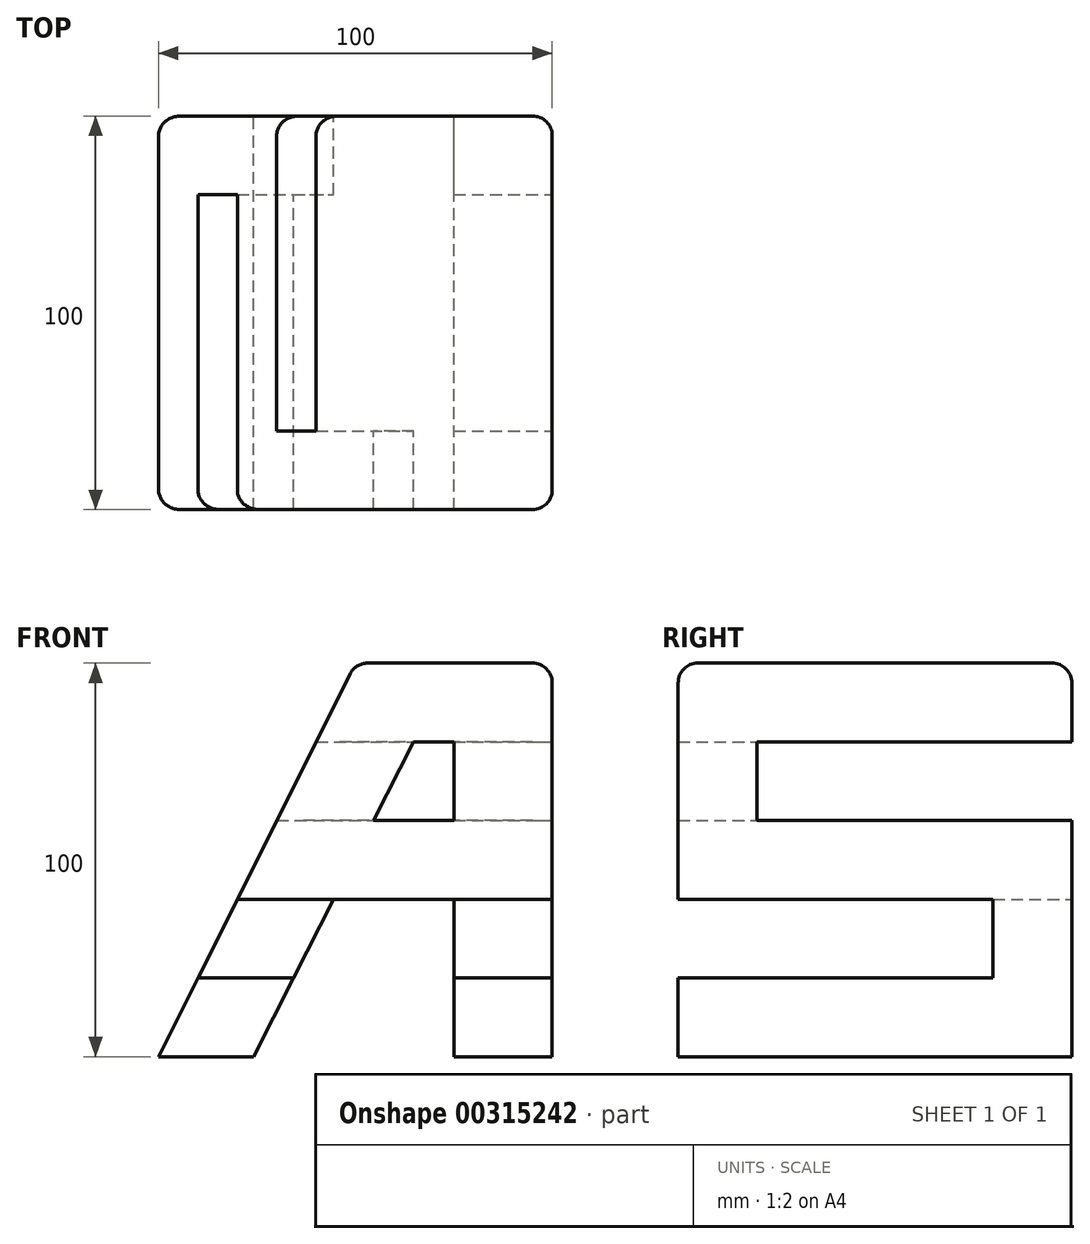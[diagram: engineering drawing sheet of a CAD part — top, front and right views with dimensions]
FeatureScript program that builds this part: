
annotation { "Feature Type Name" : "Feature", "Feature Type Description" : "" }
export const myFeature = defineFeature(function(context is Context, id is Id, definition is map)
    precondition{}
    {
        {
            var Q0;
            Q0=qCreatedBy(makeId("Front.planeOp"),FACE);
            var sketch = newSketch(context, id + "F0", { "sketchPlane" : qUnion([Q0])});
            skLineSegment(sketch, "E0.top", {"start": v(-50, -50) * mm, "end": v(-25.92, -50) * mm});
            skLineSegment(sketch, "E0.right", {"start": v(50, 50) * mm, "end": v(50, 30) * mm});
            skPoint(sketch, "E0.middle", {"position": v(0, 0) * mm});
            skLineSegment(sketch, "E1", {"start": v(0, 50) * mm, "end": v(25, 50) * mm});
            skLineSegment(sketch, "E2", {"start": v(0, 50) * mm, "end": v(-50, -50) * mm});
            skLineSegment(sketch, "E3", {"start": v(25, 50) * mm, "end": v(50, 50) * mm});
            skLineSegment(sketch, "E4", {"start": v(50, -30) * mm, "end": v(50, -50) * mm});
            skLineSegment(sketch, "E5", {"start": v(50, -10) * mm, "end": v(50, -30) * mm});
            skLineSegment(sketch, "E6", {"start": v(50, 10) * mm, "end": v(50, -10) * mm});
            skLineSegment(sketch, "E7", {"start": v(50, 30) * mm, "end": v(50, 10) * mm});
            skLineSegment(sketch, "E8", {"start": v(-5.55, -10) * mm, "end": v(-15.73, -30) * mm});
            skLineSegment(sketch, "E9", {"start": v(-15.73, -30) * mm, "end": v(-25.92, -50) * mm});
            skLineSegment(sketch, "E10", {"start": v(25, 30) * mm, "end": v(25, 10) * mm});
            skLineSegment(sketch, "E11", {"start": v(25, 10) * mm, "end": v(4.63, 10) * mm});
            skLineSegment(sketch, "E12", {"start": v(25, -10) * mm, "end": v(25, -30) * mm});
            skLineSegment(sketch, "E13", {"start": v(25, -30) * mm, "end": v(25, -50) * mm});
            skLineSegment(sketch, "E14", {"start": v(14.82, 30) * mm, "end": v(4.63, 10) * mm});
            skLineSegment(sketch, "E15", {"start": v(25, 30) * mm, "end": v(14.82, 30) * mm});
            skLineSegment(sketch, "E16", {"start": v(25, -10) * mm, "end": v(-5.55, -10) * mm});
            skLineSegment(sketch, "E17", {"start": v(25, -50) * mm, "end": v(50, -50) * mm});
            skSolve(sketch);
        }
        {
            var Q0;
            Q0=makeQuery(id+"F0.imprint","IMPRINT",FACE,{"disambiguationData":[TD([[makeQuery(id+"F0.imprint","IMPRINT",EDGE,{"derivedFrom":sQuery(id+"F0.wireOp",EDGE,"E0.top")}),1.0]])]});
            extrude(context, id + "F1", {"entities" : qUnion([Q0]), "depth" : 100 * mm});
        }
        {
            var Q0;
            Q0=makeQuery(id+"F1.opExtrude","SWEPT_FACE",FACE,{"disambiguationData":[OSD([sQuery(id+"F0.wireOp",EDGE,"E0.right"),sQuery(id+"F0.wireOp",EDGE,"E4"),sQuery(id+"F0.wireOp",EDGE,"E5"),sQuery(id+"F0.wireOp",EDGE,"E6"),sQuery(id+"F0.wireOp",EDGE,"E7")])]});
            var sketch = newSketch(context, id + "F2", { "sketchPlane" : qUnion([Q0])});
            skLineSegment(sketch, "E18.bottom", {"start": v(-100, -30) * mm, "end": v(-20, -30) * mm});
            skLineSegment(sketch, "E18.top", {"start": v(-100, -10) * mm, "end": v(-20, -10) * mm});
            skLineSegment(sketch, "E18.left", {"start": v(-100, -30) * mm, "end": v(-100, -10) * mm});
            skLineSegment(sketch, "E18.right", {"start": v(-20, -30) * mm, "end": v(-20, -10) * mm});
            skSolve(sketch);
        }
        {
            var Q0;
            Q0=makeQuery(id+"F2.imprint","IMPRINT",FACE,{"disambiguationData":[TD([[makeQuery(id+"F2.imprint","IMPRINT",EDGE,{"derivedFrom":sQuery(id+"F2.wireOp",EDGE,"E18.bottom")}),1.0]])]});
            extrude(context, id + "F3", {"entities" : qUnion([Q0]), "operationType" : NewBodyOperationType.REMOVE, "oppositeDirection" : true, "depth" : 100 * mm});
        }
        {
            var Q0;
            Q0=makeQuery(id+"F1.opExtrude","SWEPT_FACE",FACE,{"disambiguationData":[OSD([sQuery(id+"F0.wireOp",EDGE,"E0.right"),sQuery(id+"F0.wireOp",EDGE,"E4"),sQuery(id+"F0.wireOp",EDGE,"E5"),sQuery(id+"F0.wireOp",EDGE,"E6"),sQuery(id+"F0.wireOp",EDGE,"E7")])]});
            var sketch = newSketch(context, id + "F4", { "sketchPlane" : qUnion([Q0])});
            skLineSegment(sketch, "E19.bottom", {"start": v(0, 30) * mm, "end": v(-80, 30) * mm});
            skLineSegment(sketch, "E19.top", {"start": v(0, 10) * mm, "end": v(-80, 10) * mm});
            skLineSegment(sketch, "E19.left", {"start": v(0, 30) * mm, "end": v(0, 10) * mm});
            skLineSegment(sketch, "E19.right", {"start": v(-80, 30) * mm, "end": v(-80, 10) * mm});
            skSolve(sketch);
        }
        {
            var Q0;
            Q0=makeQuery(id+"F4.imprint","IMPRINT",FACE,{"disambiguationData":[TD([[makeQuery(id+"F4.imprint","IMPRINT",EDGE,{"derivedFrom":sQuery(id+"F4.wireOp",EDGE,"E19.bottom")}),1.0]])]});
            extrude(context, id + "F5", {"entities" : qUnion([Q0]), "operationType" : NewBodyOperationType.REMOVE, "oppositeDirection" : true, "depth" : 100 * mm});
        }
        {
            var Q0;
            {var subQ0=sQuery(id+"F0.wireOp",EDGE,"E17");var subQ1=sQuery(id+"F0.wireOp",EDGE,"E7");var subQ2=sQuery(id+"F0.wireOp",EDGE,"E6");var subQ3=sQuery(id+"F0.wireOp",EDGE,"E5");var subQ4=sQuery(id+"F0.wireOp",EDGE,"E4");var subQ5=sQuery(id+"F0.wireOp",EDGE,"E0.right");Q0=makeQuery(id+"F3.boolean.opBoolean","SPLIT",EDGE,{"disambiguationData":[TD([makeQuery(id+"F1.opExtrude","SWEPT_FACE",FACE,{"disambiguationData":[OSD([subQ0])]})])],"derivedFrom":makeQuery(id+"F1.opExtrude","CAP_EDGE",EDGE,{"disambiguationData":[OSD([subQ5,subQ4,subQ3,subQ2,subQ1])],"isStart":false})});}
            var Q1;
            {var subQ2=sQuery(id+"F0.wireOp",EDGE,"E7");var subQ3=sQuery(id+"F0.wireOp",EDGE,"E6");var subQ4=sQuery(id+"F0.wireOp",EDGE,"E5");var subQ5=sQuery(id+"F0.wireOp",EDGE,"E4");var subQ6=sQuery(id+"F0.wireOp",EDGE,"E0.right");var subQ7=sQuery(id+"F0.wireOp",EDGE,"E16");Q1=makeQuery(id+"F3.boolean.opBoolean","SPLIT",EDGE,{"disambiguationData":[TD([makeQuery(id+"F1.opExtrude","SWEPT_FACE",FACE,{"disambiguationData":[OSD([subQ7])]})])],"derivedFrom":makeQuery(id+"F1.opExtrude","CAP_EDGE",EDGE,{"disambiguationData":[OSD([subQ6,subQ5,subQ4,subQ3,subQ2])],"isStart":false})});}
            var Q2;
            Q2=makeQuery(id+"F1.opExtrude","SWEPT_EDGE",EDGE,{"disambiguationData":[OSD([sQuery(id+"F0.wireOp",EDGE,"E0.right"),sQuery(id+"F0.wireOp",EDGE,"E3")])]});
            var Q3;
            Q3=makeQuery(id+"F1.opExtrude","CAP_EDGE",EDGE,{"disambiguationData":[OSD([sQuery(id+"F0.wireOp",EDGE,"E1"),sQuery(id+"F0.wireOp",EDGE,"E3")])],"isStart":false});
            var Q4;
            Q4=makeQuery(id+"F1.opExtrude","SWEPT_EDGE",EDGE,{"disambiguationData":[OSD([sQuery(id+"F0.wireOp",EDGE,"E1"),sQuery(id+"F0.wireOp",EDGE,"E2")])]});
            var Q5;
            {var subQ0=sQuery(id+"F0.wireOp",EDGE,"E2");var subQ3=sQuery(id+"F0.wireOp",EDGE,"E16");Q5=makeQuery(id+"F3.boolean.opBoolean","SPLIT",EDGE,{"disambiguationData":[TD([makeQuery(id+"F1.opExtrude","SWEPT_FACE",FACE,{"disambiguationData":[OSD([subQ3])]})])],"derivedFrom":makeQuery(id+"F1.opExtrude","CAP_EDGE",EDGE,{"disambiguationData":[OSD([subQ0])],"isStart":false})});}
            var Q6;
            {var subQ0=sQuery(id+"F0.wireOp",EDGE,"E0.top");var subQ1=sQuery(id+"F0.wireOp",EDGE,"E2");Q6=makeQuery(id+"F3.boolean.opBoolean","SPLIT",EDGE,{"disambiguationData":[TD([makeQuery(id+"F1.opExtrude","SWEPT_FACE",FACE,{"disambiguationData":[OSD([subQ0])]})])],"derivedFrom":makeQuery(id+"F1.opExtrude","CAP_EDGE",EDGE,{"disambiguationData":[OSD([subQ1])],"isStart":false})});}
            var Q7;
            {var subQ1=sQuery(id+"F0.wireOp",EDGE,"E11");var subQ2=sQuery(id+"F0.wireOp",EDGE,"E7");var subQ3=sQuery(id+"F0.wireOp",EDGE,"E6");var subQ4=sQuery(id+"F0.wireOp",EDGE,"E5");var subQ5=sQuery(id+"F0.wireOp",EDGE,"E4");var subQ6=sQuery(id+"F0.wireOp",EDGE,"E0.right");Q7=makeQuery(id+"F5.boolean.opBoolean","SPLIT",EDGE,{"disambiguationData":[TD([makeQuery(id+"F1.opExtrude","SWEPT_FACE",FACE,{"disambiguationData":[OSD([subQ1])]})])],"derivedFrom":makeQuery(id+"F1.opExtrude","CAP_EDGE",EDGE,{"disambiguationData":[OSD([subQ6,subQ5,subQ4,subQ3,subQ2])],"isStart":true})});}
            var Q8;
            {var subQ2=sQuery(id+"F0.wireOp",EDGE,"E7");var subQ3=sQuery(id+"F0.wireOp",EDGE,"E6");var subQ4=sQuery(id+"F0.wireOp",EDGE,"E5");var subQ5=sQuery(id+"F0.wireOp",EDGE,"E4");var subQ6=sQuery(id+"F0.wireOp",EDGE,"E0.right");var subQ7=sQuery(id+"F0.wireOp",EDGE,"E15");Q8=makeQuery(id+"F5.boolean.opBoolean","SPLIT",EDGE,{"disambiguationData":[TD([makeQuery(id+"F1.opExtrude","SWEPT_FACE",FACE,{"disambiguationData":[OSD([subQ7])]})])],"derivedFrom":makeQuery(id+"F1.opExtrude","CAP_EDGE",EDGE,{"disambiguationData":[OSD([subQ6,subQ5,subQ4,subQ3,subQ2])],"isStart":true})});}
            var Q9;
            {var subQ1=sQuery(id+"F0.wireOp",EDGE,"E2");var subQ2=sQuery(id+"F0.wireOp",EDGE,"E0.top");Q9=makeQuery(id+"F5.boolean.opBoolean","SPLIT",EDGE,{"disambiguationData":[TD([makeQuery(id+"F1.opExtrude","SWEPT_FACE",FACE,{"disambiguationData":[OSD([subQ2])]})])],"derivedFrom":makeQuery(id+"F1.opExtrude","CAP_EDGE",EDGE,{"disambiguationData":[OSD([subQ1])],"isStart":true})});}
            var Q10;
            {var subQ0=sQuery(id+"F0.wireOp",EDGE,"E2");var subQ3=sQuery(id+"F0.wireOp",EDGE,"E15");Q10=makeQuery(id+"F5.boolean.opBoolean","SPLIT",EDGE,{"disambiguationData":[TD([makeQuery(id+"F1.opExtrude","SWEPT_FACE",FACE,{"disambiguationData":[OSD([subQ3])]})])],"derivedFrom":makeQuery(id+"F1.opExtrude","CAP_EDGE",EDGE,{"disambiguationData":[OSD([subQ0])],"isStart":true})});}
            var Q11;
            Q11=makeQuery(id+"F1.opExtrude","CAP_EDGE",EDGE,{"disambiguationData":[OSD([sQuery(id+"F0.wireOp",EDGE,"E1"),sQuery(id+"F0.wireOp",EDGE,"E3")])],"isStart":true});
            fillet(context, id + "F6", {"entities" : qUnion([Q0, Q1, Q2, Q3, Q4, Q5, Q6, Q7, Q8, Q9, Q10, Q11]), "radius" : 5 * mm, "tangentPropagation" : true, "allowEdgeOverflow" : false});
        }
    });
